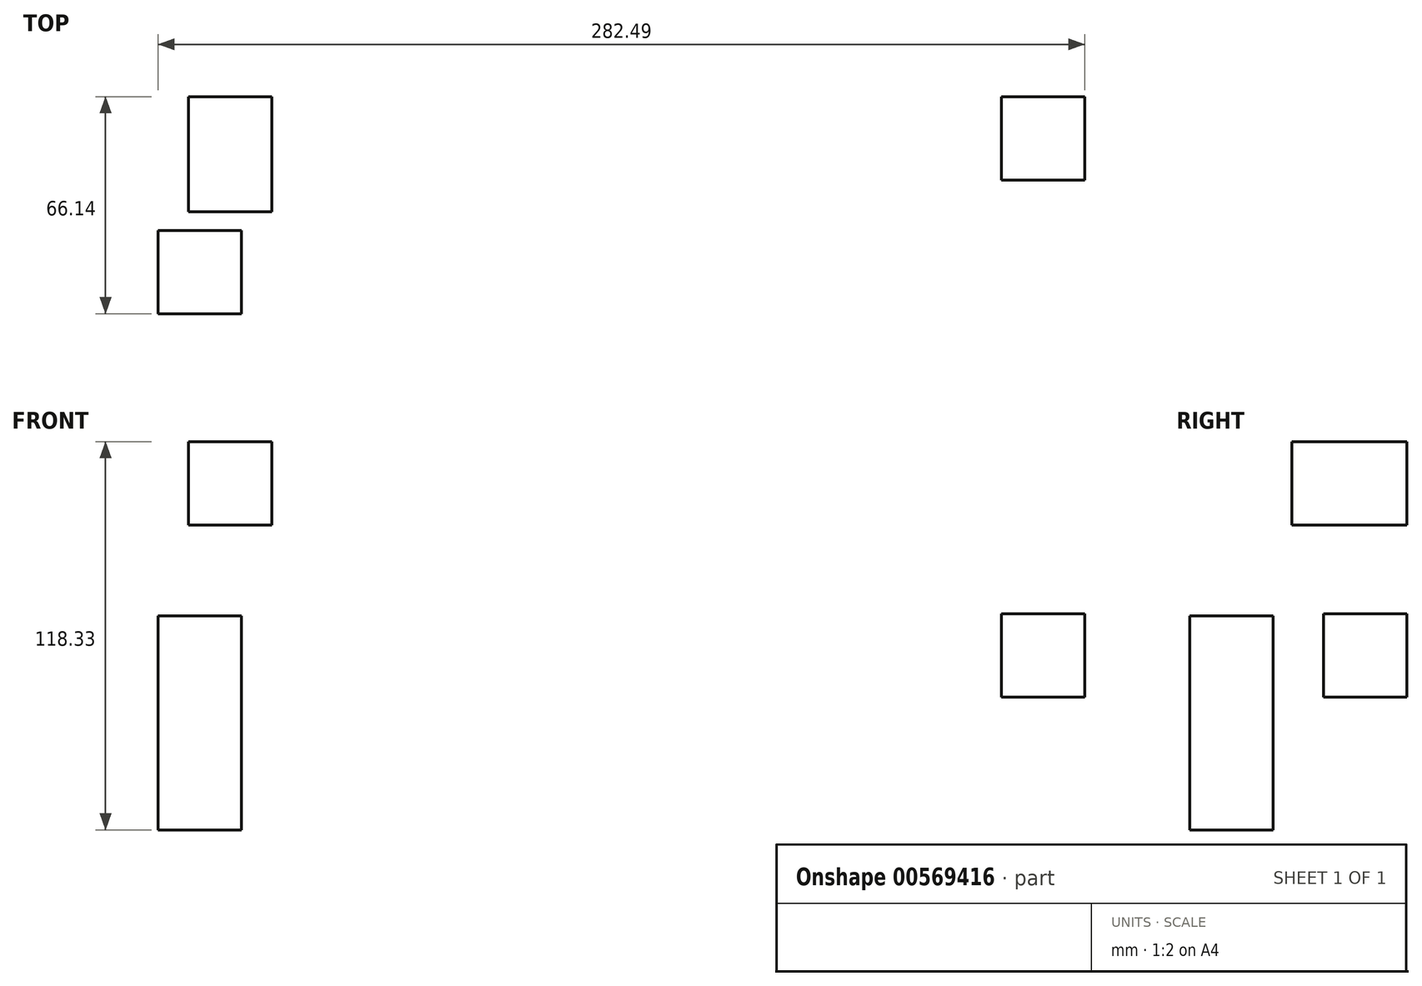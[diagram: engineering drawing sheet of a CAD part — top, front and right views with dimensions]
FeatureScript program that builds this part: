
annotation { "Feature Type Name" : "Feature", "Feature Type Description" : "" }
export const myFeature = defineFeature(function(context is Context, id is Id, definition is map)
    precondition{}
    {
        {
            var Q0;
            Q0=qCreatedBy(makeId("Front.planeOp"),FACE);
            var sketch = newSketch(context, id + "F0", { "sketchPlane" : qUnion([Q0])});
            skLineSegment(sketch, "E0.bottom", {"start": v(-123.65, 53.05) * mm, "end": v(-98.25, 53.05) * mm});
            skLineSegment(sketch, "E0.top", {"start": v(-123.65, 27.65) * mm, "end": v(-98.25, 27.65) * mm});
            skLineSegment(sketch, "E0.left", {"start": v(-123.65, 53.05) * mm, "end": v(-123.65, 27.65) * mm});
            skLineSegment(sketch, "E0.right", {"start": v(-98.25, 53.05) * mm, "end": v(-98.25, 27.65) * mm});
            skSolve(sketch);
        }
        {
            var Q0;
            Q0=makeQuery(id+"F0.imprint","IMPRINT",FACE,{"disambiguationData":[TD([[makeQuery(id+"F0.imprint","IMPRINT",EDGE,{"derivedFrom":sQuery(id+"F0.wireOp",EDGE,"E0.bottom")}),-1.0]])]});
            extrude(context, id + "F1", {"entities" : qUnion([Q0]), "depth" : 35.05 * mm, "offsetDistance" : 25.4 * mm});
        }
        {
            var Q0;
            Q0=qCreatedBy(makeId("Top.planeOp"),FACE);
            var sketch = newSketch(context, id + "F2", { "sketchPlane" : qUnion([Q0])});
            skLineSegment(sketch, "E1.bottom", {"start": v(-132.9, -40.74) * mm, "end": v(-107.5, -40.74) * mm});
            skLineSegment(sketch, "E1.top", {"start": v(-132.9, -66.14) * mm, "end": v(-107.5, -66.14) * mm});
            skLineSegment(sketch, "E1.left", {"start": v(-132.9, -40.74) * mm, "end": v(-132.9, -66.14) * mm});
            skLineSegment(sketch, "E1.right", {"start": v(-107.5, -40.74) * mm, "end": v(-107.5, -66.14) * mm});
            skSolve(sketch);
        }
        {
            var Q0;
            Q0 = qSketchRegion(id + "F2", true);
            extrude(context, id + "F3", {"entities" : qUnion([Q0]), "oppositeDirection" : true, "depth" : 65.28 * mm, "offsetDistance" : 25.4 * mm});
        }
        {
            var Q0;
            Q0=qCreatedBy(makeId("Front.planeOp"),FACE);
            var sketch = newSketch(context, id + "F4", { "sketchPlane" : qUnion([Q0])});
            skLineSegment(sketch, "E2.bottom", {"start": v(124.2, 0.55) * mm, "end": v(149.6, 0.55) * mm});
            skLineSegment(sketch, "E2.top", {"start": v(124.2, -24.85) * mm, "end": v(149.6, -24.85) * mm});
            skLineSegment(sketch, "E2.left", {"start": v(124.2, 0.55) * mm, "end": v(124.2, -24.85) * mm});
            skLineSegment(sketch, "E2.right", {"start": v(149.6, 0.55) * mm, "end": v(149.6, -24.85) * mm});
            skSolve(sketch);
        }
        {
            var Q0;
            Q0=makeQuery(id+"F4.imprint","IMPRINT",FACE,{"disambiguationData":[TD([[makeQuery(id+"F4.imprint","IMPRINT",EDGE,{"derivedFrom":sQuery(id+"F4.wireOp",EDGE,"E2.bottom")}),-1.0]])]});
            extrude(context, id + "F5", {"entities" : qUnion([Q0]), "depth" : 25.4 * mm, "offsetDistance" : 25.4 * mm});
        }
    });
